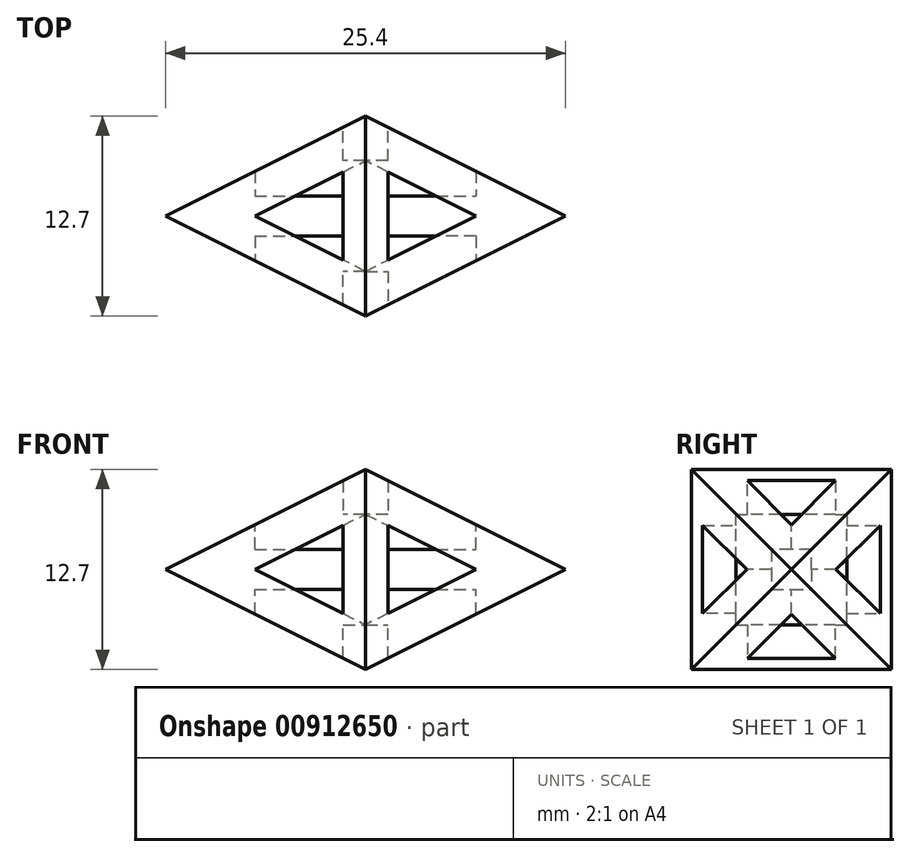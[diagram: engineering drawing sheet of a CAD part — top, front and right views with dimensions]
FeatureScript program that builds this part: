
annotation { "Feature Type Name" : "Feature", "Feature Type Description" : "" }
export const myFeature = defineFeature(function(context is Context, id is Id, definition is map)
    precondition{}
    {
        {
            var Q0;
            Q0=qCreatedBy(makeId("Right.planeOp"),FACE);
            var sketch = newSketch(context, id + "F0", { "sketchPlane" : qUnion([Q0])});
            skLineSegment(sketch, "E0.bottom", {"start": v(6.35, -6.35) * mm, "end": v(-6.35, -6.35) * mm});
            skLineSegment(sketch, "E0.top", {"start": v(6.35, 6.35) * mm, "end": v(-6.35, 6.35) * mm});
            skLineSegment(sketch, "E0.left", {"start": v(6.35, -6.35) * mm, "end": v(6.35, 6.35) * mm});
            skLineSegment(sketch, "E0.right", {"start": v(-6.35, -6.35) * mm, "end": v(-6.35, 6.35) * mm});
            skPoint(sketch, "E0.middle", {"position": v(0, 0) * mm});
            skSolve(sketch);
        }
        {
            var Q0;
            Q0=makeQuery(id+"F0.imprint","IMPRINT",FACE,{"disambiguationData":[TD([[makeQuery(id+"F0.imprint","IMPRINT",EDGE,{"derivedFrom":sQuery(id+"F0.wireOp",EDGE,"E0.bottom")}),-1.0]])]});
            extrude(context, id + "F1", {"entities" : qUnion([Q0]), "depth" : 25.4 * mm, "offsetDistance" : 25.4 * mm});
        }
        {
            var Q0;
            Q0=makeQuery(id+"F1.opExtrude","SWEPT_FACE",FACE,{"disambiguationData":[OSD([sQuery(id+"F0.wireOp",EDGE,"E0.right")])]});
            var sketch = newSketch(context, id + "F2", { "sketchPlane" : qUnion([Q0])});
            skLineSegment(sketch, "E1", {"start": v(0, 0) * mm, "end": v(12.7, -6.35) * mm});
            skLineSegment(sketch, "E2", {"start": v(12.7, -6.35) * mm, "end": v(25.4, 0) * mm});
            skLineSegment(sketch, "E3", {"start": v(25.4, 0) * mm, "end": v(12.7, 6.35) * mm});
            skLineSegment(sketch, "E4", {"start": v(12.7, 6.35) * mm, "end": v(0, 0) * mm});
            skLineSegment(sketch, "E5", {"start": v(5.68, 0) * mm, "end": v(11.43, -2.88) * mm});
            skLineSegment(sketch, "E6", {"start": v(11.43, -2.88) * mm, "end": v(11.43, 2.88) * mm});
            skLineSegment(sketch, "E7", {"start": v(11.43, 2.88) * mm, "end": v(5.68, 0) * mm});
            skLineSegment(sketch, "E8", {"start": v(13.97, -2.88) * mm, "end": v(13.97, 2.88) * mm});
            skLineSegment(sketch, "E9", {"start": v(13.97, 2.88) * mm, "end": v(19.72, 0) * mm});
            skLineSegment(sketch, "E10", {"start": v(19.72, 0) * mm, "end": v(13.97, -2.88) * mm});
            skLineSegment(sketch, "E11", {"start": v(11.43, 2.88) * mm, "end": v(12.7, 3.51) * mm});
            skLineSegment(sketch, "E12", {"start": v(13.97, 2.88) * mm, "end": v(12.7, 3.51) * mm});
            skLineSegment(sketch, "E13", {"start": v(11.43, -2.88) * mm, "end": v(12.7, -3.51) * mm});
            skLineSegment(sketch, "E14", {"start": v(13.97, -2.88) * mm, "end": v(12.7, -3.51) * mm});
            skPoint(sketch, "E14.endSnap0", {"position": v(12.45, -3.38) * mm});
            skPoint(sketch, "E15.orphan", {"position": v(12.45, -3.64) * mm});
            skPoint(sketch, "E16.orphan", {"position": v(13.46, -3.9) * mm});
            skSolve(sketch);
        }
        {
            var Q0;
            Q0=makeQuery(id+"F1.opExtrude","SWEPT_FACE",FACE,{"disambiguationData":[OSD([sQuery(id+"F0.wireOp",EDGE,"E0.top")])]});
            var sketch = newSketch(context, id + "F3", { "sketchPlane" : qUnion([Q0])});
            skLineSegment(sketch, "E17", {"start": v(0, 0) * mm, "end": v(12.7, 6.35) * mm});
            skLineSegment(sketch, "E18", {"start": v(12.7, 6.35) * mm, "end": v(25.4, 0) * mm});
            skLineSegment(sketch, "E19", {"start": v(25.4, 0) * mm, "end": v(12.7, -6.35) * mm});
            skLineSegment(sketch, "E20", {"start": v(12.7, -6.35) * mm, "end": v(0, 0) * mm});
            skLineSegment(sketch, "E21", {"start": v(5.68, 0) * mm, "end": v(12.7, 3.51) * mm});
            skLineSegment(sketch, "E22", {"start": v(12.7, 3.51) * mm, "end": v(19.72, 0) * mm});
            skLineSegment(sketch, "E23", {"start": v(19.72, 0) * mm, "end": v(12.7, -3.51) * mm});
            skLineSegment(sketch, "E24", {"start": v(12.7, -3.51) * mm, "end": v(5.68, 0) * mm});
            skLineSegment(sketch, "E25", {"start": v(13.97, 2.88) * mm, "end": v(13.97, -2.88) * mm});
            skLineSegment(sketch, "E26", {"start": v(11.43, 2.88) * mm, "end": v(11.43, -2.88) * mm});
            skSolve(sketch);
        }
        {
            var Q0;
            Q0=makeQuery(id+"F1.opExtrude","CAP_FACE",FACE,{"disambiguationData":[OSD([sQuery(id+"F0.wireOp",EDGE,"E0.bottom"),sQuery(id+"F0.wireOp",EDGE,"E0.top"),sQuery(id+"F0.wireOp",EDGE,"E0.left"),sQuery(id+"F0.wireOp",EDGE,"E0.right")])],"isStart":false});
            var sketch = newSketch(context, id + "F4", { "sketchPlane" : qUnion([Q0])});
            skLineSegment(sketch, "E27.bottom", {"start": v(-1.27, -1.27) * mm, "end": v(1.27, -1.27) * mm});
            skLineSegment(sketch, "E27.top", {"start": v(-1.27, 1.27) * mm, "end": v(1.27, 1.27) * mm});
            skLineSegment(sketch, "E27.left", {"start": v(-1.27, -1.27) * mm, "end": v(-1.27, 1.27) * mm});
            skLineSegment(sketch, "E27.right", {"start": v(1.27, -1.27) * mm, "end": v(1.27, 1.27) * mm});
            skPoint(sketch, "E27.middle", {"position": v(0, 0) * mm});
            skSolve(sketch);
        }
        {
            var Q0;
            {var subQ3=sQuery(id+"F3.wireOp",EDGE,"E25");Q0=makeQuery(id+"F3.imprint","IMPRINT",FACE,{"disambiguationData":[TD([[makeQuery(id+"F3.imprint","IMPRINT",EDGE,{"derivedFrom":subQ3}),1.0]])]});}
            var Q1;
            {var subQ3=sQuery(id+"F3.wireOp",EDGE,"E25");Q1=makeQuery(id+"F3.imprint","IMPRINT",FACE,{"disambiguationData":[TD([[makeQuery(id+"F3.imprint","IMPRINT",EDGE,{"derivedFrom":subQ3}),-1.0]])]});}
            var Q2;
            {var subQ3=sQuery(id+"F3.wireOp",EDGE,"E26");Q2=makeQuery(id+"F3.imprint","IMPRINT",FACE,{"disambiguationData":[TD([[makeQuery(id+"F3.imprint","IMPRINT",EDGE,{"derivedFrom":subQ3}),-1.0]])]});}
            extrude(context, id + "F5", {"entities" : qUnion([Q0, Q1, Q2]), "operationType" : NewBodyOperationType.REMOVE, "oppositeDirection" : true, "depth" : 12.7 * mm, "offsetDistance" : 25.4 * mm});
        }
        {
            var Q0;
            Q0=makeQuery(id+"F2.imprint","IMPRINT",FACE,{"disambiguationData":[TD([[makeQuery(id+"F2.imprint","IMPRINT",EDGE,{"derivedFrom":sQuery(id+"F2.wireOp",EDGE,"E8")}),-1.0]])]});
            var Q1;
            Q1=makeQuery(id+"F2.imprint","IMPRINT",FACE,{"disambiguationData":[TD([[makeQuery(id+"F2.imprint","IMPRINT",EDGE,{"derivedFrom":sQuery(id+"F2.wireOp",EDGE,"E6")}),-1.0]])]});
            var Q2;
            Q2=makeQuery(id+"F2.imprint","IMPRINT",FACE,{"disambiguationData":[TD([[makeQuery(id+"F2.imprint","IMPRINT",EDGE,{"derivedFrom":sQuery(id+"F2.wireOp",EDGE,"E5")}),1.0]])]});
            extrude(context, id + "F6", {"entities" : qUnion([Q0, Q1, Q2]), "operationType" : NewBodyOperationType.REMOVE, "oppositeDirection" : true, "depth" : 12.7 * mm, "offsetDistance" : 25.4 * mm});
        }
        {
            var Q0;
            Q0=makeQuery(id+"F4.imprint","IMPRINT",FACE,{"disambiguationData":[TD([[makeQuery(id+"F4.imprint","IMPRINT",EDGE,{"derivedFrom":sQuery(id+"F4.wireOp",EDGE,"E27.bottom")}),1.0]])]});
            extrude(context, id + "F7", {"entities" : qUnion([Q0]), "operationType" : NewBodyOperationType.ADD, "depth" : 0 * mm, "offsetDistance" : 25.4 * mm, "hasSecondDirection" : true, "secondDirectionOppositeDirection" : true, "secondDirectionDepth" : 25.4 * mm});
        }
        {
            var Q0;
            Q0=makeQuery(id+"F1.opExtrude","SWEPT_FACE",FACE,{"disambiguationData":[OSD([sQuery(id+"F0.wireOp",EDGE,"E0.top")])]});
            var sketch = newSketch(context, id + "F8", { "sketchPlane" : qUnion([Q0])});
            skLineSegment(sketch, "E28.bottom", {"start": v(11.28, 6.35) * mm, "end": v(14.12, 6.35) * mm});
            skLineSegment(sketch, "E28.top", {"start": v(11.28, 3.51) * mm, "end": v(14.12, 3.51) * mm});
            skLineSegment(sketch, "E28.left", {"start": v(11.28, 6.35) * mm, "end": v(11.28, 3.51) * mm});
            skLineSegment(sketch, "E28.right", {"start": v(14.12, 6.35) * mm, "end": v(14.12, 3.51) * mm});
            skLineSegment(sketch, "E29.bottom", {"start": v(11.28, -3.51) * mm, "end": v(14.12, -3.51) * mm});
            skLineSegment(sketch, "E29.top", {"start": v(11.28, -6.35) * mm, "end": v(14.12, -6.35) * mm});
            skLineSegment(sketch, "E29.left", {"start": v(11.28, -3.51) * mm, "end": v(11.28, -6.35) * mm});
            skLineSegment(sketch, "E29.right", {"start": v(14.12, -3.51) * mm, "end": v(14.12, -6.35) * mm});
            skSolve(sketch);
        }
        {
            var Q0;
            Q0=makeQuery(id+"F8.imprint","IMPRINT",FACE,{"disambiguationData":[TD([[makeQuery(id+"F8.imprint","IMPRINT",EDGE,{"derivedFrom":sQuery(id+"F8.wireOp",EDGE,"E28.bottom")}),1.0]])]});
            var Q1;
            Q1=makeQuery(id+"F8.imprint","IMPRINT",FACE,{"disambiguationData":[TD([[makeQuery(id+"F8.imprint","IMPRINT",EDGE,{"derivedFrom":sQuery(id+"F8.wireOp",EDGE,"E29.top")}),-1.0]])]});
            extrude(context, id + "F9", {"entities" : qUnion([Q0, Q1]), "operationType" : NewBodyOperationType.ADD, "oppositeDirection" : true, "depth" : 12.7 * mm, "offsetDistance" : 25.4 * mm});
        }
        {
            var Q0;
            Q0=makeQuery(id+"F9.boolean.opBoolean","MERGE",FACE,{"derivedFrom":[makeQuery(id+"F1.opExtrude","SWEPT_FACE",FACE,{"disambiguationData":[OSD([sQuery(id+"F0.wireOp",EDGE,"E0.right")])]}),makeQuery(id+"F9.opExtrude","SWEPT_FACE",FACE,{"disambiguationData":[OSD([sQuery(id+"F8.wireOp",EDGE,"E29.top")])]})]});
            var sketch = newSketch(context, id + "F10", { "sketchPlane" : qUnion([Q0])});
            skLineSegment(sketch, "E30.bottom", {"start": v(11.28, -6.35) * mm, "end": v(14.12, -6.35) * mm});
            skLineSegment(sketch, "E30.top", {"start": v(11.28, -3.51) * mm, "end": v(14.12, -3.51) * mm});
            skLineSegment(sketch, "E30.left", {"start": v(11.28, -6.35) * mm, "end": v(11.28, -3.51) * mm});
            skLineSegment(sketch, "E30.right", {"start": v(14.12, -6.35) * mm, "end": v(14.12, -3.51) * mm});
            skLineSegment(sketch, "E31.bottom", {"start": v(14.12, 6.35) * mm, "end": v(11.28, 6.35) * mm});
            skLineSegment(sketch, "E31.top", {"start": v(14.12, 3.51) * mm, "end": v(11.28, 3.51) * mm});
            skLineSegment(sketch, "E31.left", {"start": v(14.12, 6.35) * mm, "end": v(14.12, 3.51) * mm});
            skLineSegment(sketch, "E31.right", {"start": v(11.28, 6.35) * mm, "end": v(11.28, 3.51) * mm});
            skSolve(sketch);
        }
        {
            var Q0;
            Q0=makeQuery(id+"F10.imprint","IMPRINT",FACE,{"disambiguationData":[TD([[makeQuery(id+"F10.imprint","IMPRINT",EDGE,{"derivedFrom":sQuery(id+"F10.wireOp",EDGE,"E30.bottom")}),-1.0]])]});
            var Q1;
            Q1=makeQuery(id+"F10.imprint","IMPRINT",FACE,{"disambiguationData":[TD([[makeQuery(id+"F10.imprint","IMPRINT",EDGE,{"derivedFrom":sQuery(id+"F10.wireOp",EDGE,"E31.bottom")}),1.0]])]});
            extrude(context, id + "F11", {"entities" : qUnion([Q0, Q1]), "operationType" : NewBodyOperationType.ADD, "oppositeDirection" : true, "depth" : 12.7 * mm, "offsetDistance" : 25.4 * mm});
        }
        {
            var Q0;
            {var subQ0=sQuery(id+"F2.wireOp",EDGE,"E1");Q0=makeQuery(id+"F2.imprint","IMPRINT",FACE,{"disambiguationData":[TD([[makeQuery(id+"F2.imprint","IMPRINT",EDGE,{"derivedFrom":subQ0}),-1.0]])]});}
            var Q1;
            {var subQ0=sQuery(id+"F2.wireOp",EDGE,"E4");Q1=makeQuery(id+"F2.imprint","IMPRINT",FACE,{"disambiguationData":[TD([[makeQuery(id+"F2.imprint","IMPRINT",EDGE,{"derivedFrom":subQ0}),-1.0]])]});}
            var Q2;
            {var subQ0=sQuery(id+"F2.wireOp",EDGE,"E2");Q2=makeQuery(id+"F2.imprint","IMPRINT",FACE,{"disambiguationData":[TD([[makeQuery(id+"F2.imprint","IMPRINT",EDGE,{"derivedFrom":subQ0}),-1.0]])]});}
            var Q3;
            {var subQ0=sQuery(id+"F2.wireOp",EDGE,"E3");Q3=makeQuery(id+"F2.imprint","IMPRINT",FACE,{"disambiguationData":[TD([[makeQuery(id+"F2.imprint","IMPRINT",EDGE,{"derivedFrom":subQ0}),-1.0]])]});}
            extrude(context, id + "F12", {"entities" : qUnion([Q0, Q1, Q2, Q3]), "operationType" : NewBodyOperationType.REMOVE, "endBound" : BoundingType.THROUGH_ALL, "oppositeDirection" : true, "depth" : 25.4 * mm, "offsetDistance" : 25.4 * mm});
        }
        {
            var Q0;
            {var subQ0=sQuery(id+"F3.wireOp",EDGE,"E17");Q0=makeQuery(id+"F3.imprint","IMPRINT",FACE,{"disambiguationData":[TD([[makeQuery(id+"F3.imprint","IMPRINT",EDGE,{"derivedFrom":subQ0}),1.0]])]});}
            var Q1;
            {var subQ0=sQuery(id+"F3.wireOp",EDGE,"E20");Q1=makeQuery(id+"F3.imprint","IMPRINT",FACE,{"disambiguationData":[TD([[makeQuery(id+"F3.imprint","IMPRINT",EDGE,{"derivedFrom":subQ0}),1.0]])]});}
            var Q2;
            {var subQ0=sQuery(id+"F3.wireOp",EDGE,"E19");Q2=makeQuery(id+"F3.imprint","IMPRINT",FACE,{"disambiguationData":[TD([[makeQuery(id+"F3.imprint","IMPRINT",EDGE,{"derivedFrom":subQ0}),1.0]])]});}
            var Q3;
            {var subQ0=sQuery(id+"F3.wireOp",EDGE,"E18");Q3=makeQuery(id+"F3.imprint","IMPRINT",FACE,{"disambiguationData":[TD([[makeQuery(id+"F3.imprint","IMPRINT",EDGE,{"derivedFrom":subQ0}),1.0]])]});}
            extrude(context, id + "F13", {"entities" : qUnion([Q0, Q1, Q2, Q3]), "operationType" : NewBodyOperationType.REMOVE, "oppositeDirection" : true, "depth" : 25.4 * mm, "offsetDistance" : 25.4 * mm});
        }
    });
